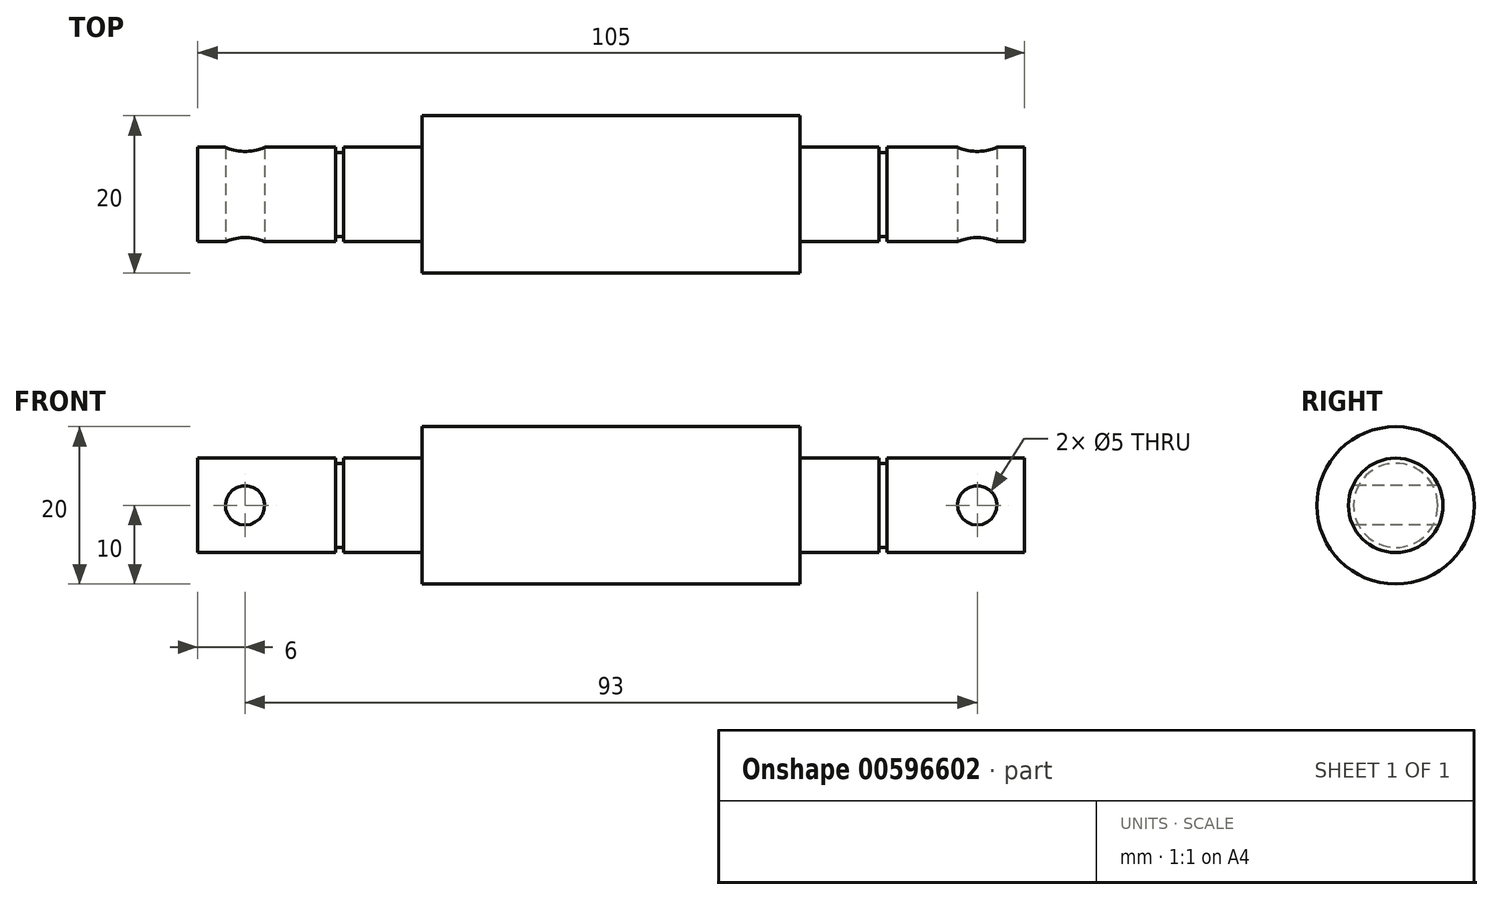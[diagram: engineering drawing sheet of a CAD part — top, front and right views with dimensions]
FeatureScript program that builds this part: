
annotation { "Feature Type Name" : "Feature", "Feature Type Description" : "" }
export const myFeature = defineFeature(function(context is Context, id is Id, definition is map)
    precondition{}
    {
        {
            var Q0;
            Q0=qCreatedBy(makeId("Front.planeOp"),FACE);
            var sketch = newSketch(context, id + "F0", { "sketchPlane" : qUnion([Q0])});
            skLineSegment(sketch, "E0", {"start": v(0, 0) * mm, "end": v(105, 0) * mm});
            skLineSegment(sketch, "E1", {"start": v(0, 0) * mm, "end": v(0, 6) * mm});
            skLineSegment(sketch, "E2", {"start": v(0, 6) * mm, "end": v(17.48, 6) * mm});
            skLineSegment(sketch, "E3", {"start": v(17.48, 6) * mm, "end": v(17.48, 5.35) * mm});
            skLineSegment(sketch, "E4", {"start": v(17.48, 5.35) * mm, "end": v(18.5, 5.35) * mm});
            skLineSegment(sketch, "E5", {"start": v(18.5, 5.35) * mm, "end": v(18.5, 6) * mm});
            skLineSegment(sketch, "E6", {"start": v(18.5, 6) * mm, "end": v(28.5, 6) * mm});
            skLineSegment(sketch, "E7", {"start": v(28.5, 6) * mm, "end": v(28.5, 10) * mm});
            skLineSegment(sketch, "E8", {"start": v(28.5, 10) * mm, "end": v(76.5, 10) * mm});
            skLineSegment(sketch, "E9", {"start": v(52.5, 10) * mm, "end": v(52.5, 2.67) * mm, "construction": true});
            skLineSegment(sketch, "E10.MirrorCS", {"start": v(76.5, 6) * mm, "end": v(76.5, 10) * mm});
            skLineSegment(sketch, "E11.MirrorCS", {"start": v(86.5, 6) * mm, "end": v(76.5, 6) * mm});
            skLineSegment(sketch, "E12.MirrorCS", {"start": v(86.5, 5.35) * mm, "end": v(86.5, 6) * mm});
            skLineSegment(sketch, "E13.MirrorCS", {"start": v(87.52, 5.35) * mm, "end": v(86.5, 5.35) * mm});
            skLineSegment(sketch, "E14.MirrorCS", {"start": v(87.52, 6) * mm, "end": v(87.52, 5.35) * mm});
            skLineSegment(sketch, "E15.MirrorCS", {"start": v(105, 6) * mm, "end": v(87.52, 6) * mm});
            skLineSegment(sketch, "E16.MirrorCS", {"start": v(105, 0) * mm, "end": v(105, 6) * mm});
            skSolve(sketch);
        }
        {
            var Q0;
            Q0 = qSketchRegion(id + "F0", true);
            var Q1;
            Q1=sQuery(id+"F0.wireOp",EDGE,"E0");
            revolve(context, id + "F1", {"entities" : qUnion([Q0]), "axis" : qUnion([Q1]), "revolveType" : RevolveType.FULL});
        }
        {
            var Q0;
            Q0=qCreatedBy(makeId("Front.planeOp"),FACE);
            cPlane(context, id + "F2", {"entities" : qUnion([Q0]), "cplaneType" : CPlaneType.OFFSET, "offset" : 6 * mm, "width" : 150 * mm, "height" : 150 * mm});
        }
        {
            var Q0;
            Q0=qCreatedBy(id+"F2.planeOp",FACE);
            var sketch = newSketch(context, id + "F3", { "sketchPlane" : qUnion([Q0])});
            skPoint(sketch, "E17", {"position": v(6, 0) * mm});
            skPoint(sketch, "E18", {"position": v(99, 0) * mm});
            skSolve(sketch);
        }
        {
            var Q0;
            Q0=sQuery(id+"F3.wireOp",VERTEX,"E17");
            var Q1;
            Q1=sQuery(id+"F3.wireOp",VERTEX,"E18");
            var Q2;
            Q2=makeQuery(id+"F1.opRevolve","SWEPT_BODY",BODY,{"disambiguationData":[OSD([sQuery(id+"F0.wireOp",EDGE,"E0"),sQuery(id+"F0.wireOp",EDGE,"E1"),sQuery(id+"F0.wireOp",EDGE,"E2"),sQuery(id+"F0.wireOp",EDGE,"E3"),sQuery(id+"F0.wireOp",EDGE,"E4"),sQuery(id+"F0.wireOp",EDGE,"E5"),sQuery(id+"F0.wireOp",EDGE,"E6"),sQuery(id+"F0.wireOp",EDGE,"E7"),sQuery(id+"F0.wireOp",EDGE,"E8"),sQuery(id+"F0.wireOp",EDGE,"E10.MirrorCS"),sQuery(id+"F0.wireOp",EDGE,"E11.MirrorCS"),sQuery(id+"F0.wireOp",EDGE,"E12.MirrorCS"),sQuery(id+"F0.wireOp",EDGE,"E13.MirrorCS"),sQuery(id+"F0.wireOp",EDGE,"E14.MirrorCS"),sQuery(id+"F0.wireOp",EDGE,"E15.MirrorCS"),sQuery(id+"F0.wireOp",EDGE,"E16.MirrorCS")])]});
            hole(context, id + "F4", {"style" : HoleStyle.SIMPLE, "endStyle" : HoleEndStyle.BLIND, "holeDiameter" : 5 * mm, "majorDiameter" : 5 * mm, "holeDepth" : 25 * mm, "isTappedThrough" : true, "tappedDepth" : 12 * mm, "tapClearance" : 3, "startFromSketch" : true, "locations" : qUnion([Q0, Q1]), "scope" : qUnion([Q2])});
        }
    });
